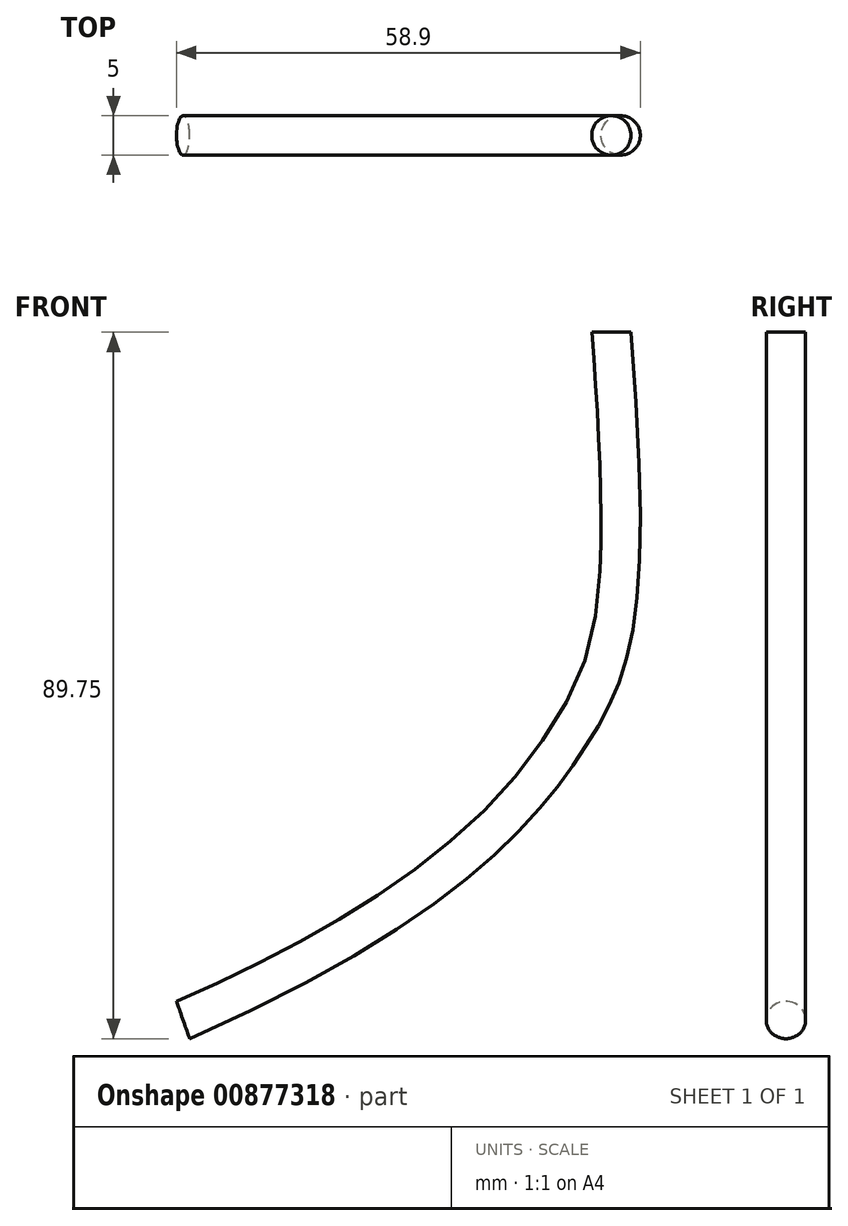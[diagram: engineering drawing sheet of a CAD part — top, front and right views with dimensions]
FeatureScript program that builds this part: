
annotation { "Feature Type Name" : "Feature", "Feature Type Description" : "" }
export const myFeature = defineFeature(function(context is Context, id is Id, definition is map)
    precondition{}
    {
        {
            var Q0;
            Q0=qCreatedBy(makeId("Top.planeOp"),FACE);
            var sketch = newSketch(context, id + "F0", { "sketchPlane" : qUnion([Q0])});
            skCircle(sketch, "E0", {"center": v(0, 0) * mm, "radius": 2.5 * mm});
            skSolve(sketch);
        }
        {
            var Q0;
            Q0=qCreatedBy(makeId("Front.planeOp"),FACE);
            var sketch = newSketch(context, id + "F1", { "sketchPlane" : qUnion([Q0])});
            skFitSpline(sketch, "E1", {"points": [v(0, 0) * mm, v(-5.18, -50.97) * mm, v(-54.4, -87.39) * mm], "startDerivative": vector(17.35, -220.89) * mm, "endDerivative": vector(-188.2, -83.14) * mm});
            skSolve(sketch);
        }
        {
            var Q0;
            Q0=qSketchRegion(id+"F0",true);
            var Q1;
            Q1=sQuery(id+"F1.wireOp",EDGE,"E1");
            sweep(context, id + "F2", {"profiles" : qUnion([Q0]), "path" : qUnion([Q1])});
        }
    });
